# Revit family: NLRS_57_DUA_UN_round-constant-volume-damper-vcmh_sacs
name_source: partatom
category: Duct Accessories
units: mm (PartAtom-declared; Revit-internal decimal feet)

## family parameters
Always vertical = No
Cut with Voids When Loaded = No
Part Type = Breaks Into
Round Connector Dimension = Use Diameter
Shared = No
Work Plane-Based = No

## types (2) — shared parameters
Assembly Code = 57.00
Description = Round Volume Damper VCMH
FireRating = 0h
IfcDescription = Round Volume Damper VCMH
IfcExportAs = IfcDamperType
IfcExportType = CONTROLDAMPER
LoadBearing = No
Manufacturer = Solid Air Climate Solutions
Model = Constant volume damper - Round
NLRS_C_content_datum_uitgifte = 29-04-2022
NLRS_C_content_provider = Solid Air Climate Systems
NLRS_C_content_versie = Versie 3.19.00
NLRS_C_description = Round Volume Damper VCMH
NLRS_C_niveau ontwikkeling = LOD400
Product_Data = VCMH_Data
SACS_Dummy = 1
Type Comments = Check flow direction!
URL = https://solid-air.nl

## per-type parameters (varying)
| type | SACS_Index2 |
| Single wall | 0 mm  [stored 0 ft] |
| Double wall | 1 mm  [stored 0.00328084 ft] |

note: [stored X ft] marks values corroborated as IEEE doubles in the binary element streams (Revit-internal decimal feet)

## geometry (parser evidence)
native form markers: Sweep x6
no freeform markers — native parametric forms only
